# Revit family: Deca_Assento termofixo com easy clean e slow close_Piano.Quadra_AP.336
name_source: partatom
category: Plumbing Fixtures
units: mm (PartAtom-declared; Revit-internal decimal feet)

## family parameters
Cut with Voids When Loaded = No
Host = Face
Part Type = Normal
Room Calculation Point = No
Round Connector Dimension = Use Diameter
Shared = No

## types (3) — shared parameters
Acompanha o Produto = FIXAÇÃO ASSENTO
Aprovado por = quattroD
Atendimento ao Cliente = 0800-0117073
Categoria = ASSENTOS
Composição Anel Vedação = -
Composição Assento = -
Composição Básica = Termofixo UF
Composição Componente = Não Possui
Consumo = -
Cor Interna = -
Cor Secundária = -
Cores Componente = Não Possui
Criado por = quattroD
Código Pai = AP.336
Description = Assento Termofixo com easy clean e slow close
Informações Complementares = -
Itens de Instalação = -
Linha = Assento Termofixo Luxo
Manufacturer = Deca
Norma = NBR-16729
Pressão máx. funcionamento = -
Pressão mín. Aquec. Acúmulo = -
Pressão mín. Aquec. Passagem = -
Pressão mín. funcionamento = -
Saída de Esgoto = -
Segmento = Banheiro Luxo
Tipo de dispositivo economizador = -
Tipo de mecanismo utilizado = -
Tipo de rosca de entrada = -
Tipo de rosca de saída = -
URL = www.deca.com.br
Vazão na Pressão máx. (L/min) = -
Vazão na Pressão mín. (L/min) = -
zero-valued in all types: Default Elevation

## per-type parameters (varying)
| type | Cor Principal | Material | Material Secundário | Model | Peso Líquido (Kg) |
| AP.336.17_Branco | Branco | Deca_Plástico - Branco | Deca_Plástico - Branco | AP.336.17 | 2.5 |
| AP.336.37_Creme | Creme | Deca_Plástico - Creme | Deca_Plástico - Creme | AP.336.37 | 1.712 |
| AP.336.95_Ébano | Ébano | Deca_Plástico - Ébano | Deca_Plástico - Ébano | AP.336.95 | 2.5 |

## geometry (parser evidence)
native form markers: Sweep x2
no freeform markers — native parametric forms only
